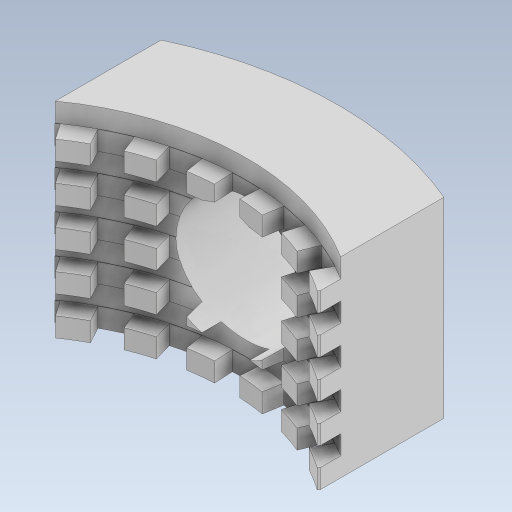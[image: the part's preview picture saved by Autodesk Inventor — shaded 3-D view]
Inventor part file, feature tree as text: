
AUTODESK INVENTOR PART (.ipt)
format: ipt  version: 2023 (Build 270158000, 158)  size: 545,280 bytes
history: native  units: in
note: dims shown in document units (in); Inventor stores cm internally (conversion verified against a paired STEP export)
features: sketch x7, extrude x6, revolve x1, plane x1, projected_geometry x1
ambient origin geometry x8: Origin, YZ Plane, XZ Plane, XY Plane, X Axis, Y Axis, Z Axis, Center Point
bodies: Solid1 (feature_tree)
feature tree (16):
  extrude  "Extrusion1"  Depth=0.2362in TaperAngle=0.0deg
  extrude  "Extrusion2"  Depth=0.3937in TaperAngle=0.0deg
  extrude  "Extrusion3"  Depth=0.0394in TaperAngle=120.0deg
  revolve  "Revolution1"  [1 undecoded]
  extrude  "Extrusion13"  Depth=0.2362in TaperAngle=0.0deg
  plane  "Work Plane5"
  extrude  "Extrusion14"  TaperAngle=0.0deg  [1 undecoded]
  extrude  "Extrusion15"  TaperAngle=0.0deg  [1 undecoded]
  sketch  "Sketch1"  dims[d0=1.0236in d1=0.2362in d2=0.0in]
  sketch  "Sketch2"  dims[d3=120.0deg d4=0.3937in d5=0.0in]
  sketch  "Sketch3"  dims[d6=0.0394in d7=7.874in d9=120.0deg]
  sketch  "Sketch4"  dims[d11=0.3937in d12=0.0in d14=3.937in d16=0.0394in d17=0.3937in d19=0.3937in]
  sketch  "Sketch25"  dims[d21=360.0deg d105=0.2362in d106=0.0in]
  projected_geometry  "Projected Loop9"
  sketch  "Sketch26"  dims[d107=0.2559in d108=0.0in d109=0.0in]
  sketch  "Sketch27"  dims[d110=0.5709in d111=0.0in d112=0.0in d91=0.0344in d92=0.0344in d93=0.0197in d94=0.0344in]
note: 3 required parameter values undecoded (feature->parameter linkage not recoverable at this tier; creation-order binding heuristic only, values carry confidence <= 0.55)